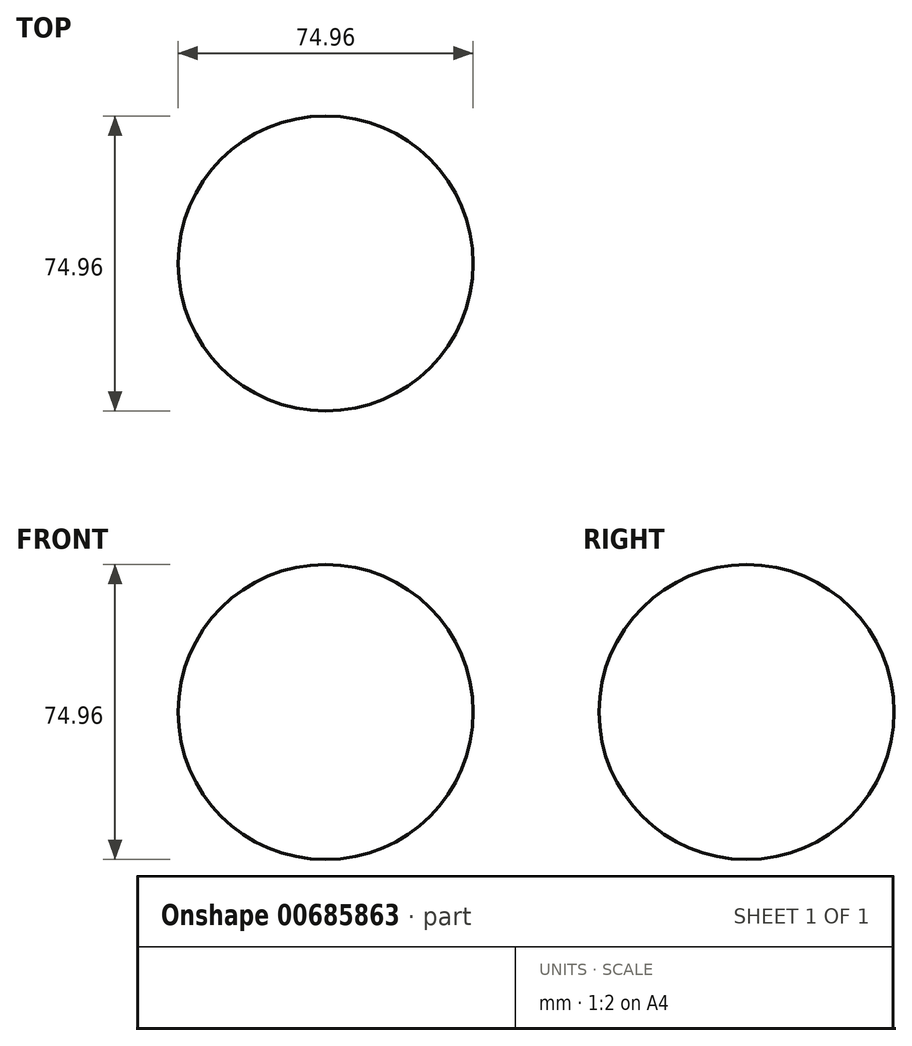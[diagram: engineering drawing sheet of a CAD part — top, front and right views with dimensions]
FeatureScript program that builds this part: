
annotation { "Feature Type Name" : "Feature", "Feature Type Description" : "" }
export const myFeature = defineFeature(function(context is Context, id is Id, definition is map)
    precondition{}
    {
        {
            var Q0;
            Q0=qCreatedBy(makeId("Top.planeOp"),FACE);
            var sketch = newSketch(context, id + "F0", { "sketchPlane" : qUnion([Q0])});
            skArc(sketch, "E0", {"start": v(0, -37.48) * mm, "mid": v(37.48, 0) * mm, "end": v(0, 37.48) * mm});
            skLineSegment(sketch, "E1", {"start": v(0, 37.48) * mm, "end": v(0, -37.48) * mm});
            skSolve(sketch);
        }
        {
            var Q0;
            Q0=makeQuery(id+"F0.imprint","IMPRINT",FACE,{"disambiguationData":[TD([[makeQuery(id+"F0.imprint","IMPRINT",EDGE,{"derivedFrom":sQuery(id+"F0.wireOp",EDGE,"E0")}),1.0]])]});
            var Q1;
            Q1=sQuery(id+"F0.wireOp",EDGE,"E1");
            revolve(context, id + "F1", {"entities" : qUnion([Q0]), "axis" : qUnion([Q1]), "revolveType" : RevolveType.FULL});
        }
    });
